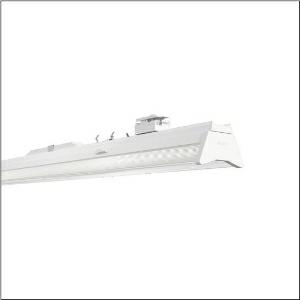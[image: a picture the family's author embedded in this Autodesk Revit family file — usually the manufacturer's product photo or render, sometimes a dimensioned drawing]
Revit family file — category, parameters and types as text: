
# Revit family: licross_r__21_performance_mo_52td167n485g_efc6
name_source: partatom
category: Lighting Fixtures
units: mm (PartAtom-declared; Revit-internal decimal feet)

## family parameters
Cut with Voids When Loaded = No
Host = Face
Light Source = No
Part Type = Normal
Room Calculation Point = No
Round Connector Dimension = Use Diameter
Shared = No

## types (1)
- Licross® 21 Performance MO (1 x LED, 8720 lm, 47.9 W, 4000K)
    Apparent Load = 48 VA
    CIE Flux Codes = 66 88 96 79 100
    Color Rendering = 80
    Color Temperature = 4000K
    Default Elevation = 1800 mm
    Description = Licross® 21 Performance MO, luminaire insert, of sheet steel, galvanised, coil coated, white, length: 1.500mm, width: 120mm, height: 123mm, LED rated luminous flux: 8.720lm, light colour: 840, control gear: ON/OFF, with plug, 3-pole, with phase selection, mains connection: 220..240V, AC, 50/60Hz, rated input power: 48W, internal wiring halogen-free, primary light control with lens, of plastic, primary optical cover: cover, of PMMA, light emission: direct/indirect distribution, primary light characteristic: symmetric, protection rating (complete): IP54, insulation class (complete): insulation class I (protective earthing), certification: CE, ENEC, UKCA, protection symbol: D if used in an environment with non-conductive dust loads with corresponding accessories, impact resistance: IK06, permissible ambient temperature for indoor applications: -35..+45°C, corresponds to IFS (International Featured Standards) requirements for safety and quality in the food industry, reducing of maximum allowable ambient temperature of 5°C with ceiling mounting, LABS conformity tested according to VDMA 24364:2018-05, packaging unit: 1 piece
    Height = 114 mm
    Lamp = 1 x LED
    Lamp Light Flux = 8720 lm
    Lamp Power = 47.9 W
    Lamp count = 1
    Length = 1500 mm
    Luminous efficacy = 182 lm/W
    Manufacturer = Siteco
    ModVariant = No
    Model = 52TD167N485G
    Mounting Place = Ceiling
    Mounting Type = Pendant
    Number of Poles = 1
    OnlyDefault = Yes
    Power Factor = 1
    Product Name = Licross® 21 Performance MO
    Product group = luminaire insert | ceiling pendant
    ProductGroupID = 902
    Protection Class = Protection class I
    Protection Degree = IP 54
    RLX_Detail_Level = 1
    RLX_Emergency_Light_Flux = 0 lm
    RLX_Emergency_Type = 0
    RLX_Emergency_Type_DB = No
    RlxData = <blob elided: 30441 chars, md5=057e5445>
    Socket = socket
    Standby Power = 0 W
    System Light Flux = 8720 lm
    System Power = 48 W
    Type Comments = Product without accessories
    Type Image = l_1256138.jpg
    URL = http://relux.com
    VarID = ---
    Voltage = 0 V
    Weight = 0.00 kg
    Width = 120 mm

## geometry (parser evidence)
native form markers: Blend x4, Sweep x12
no freeform markers — native parametric forms only
